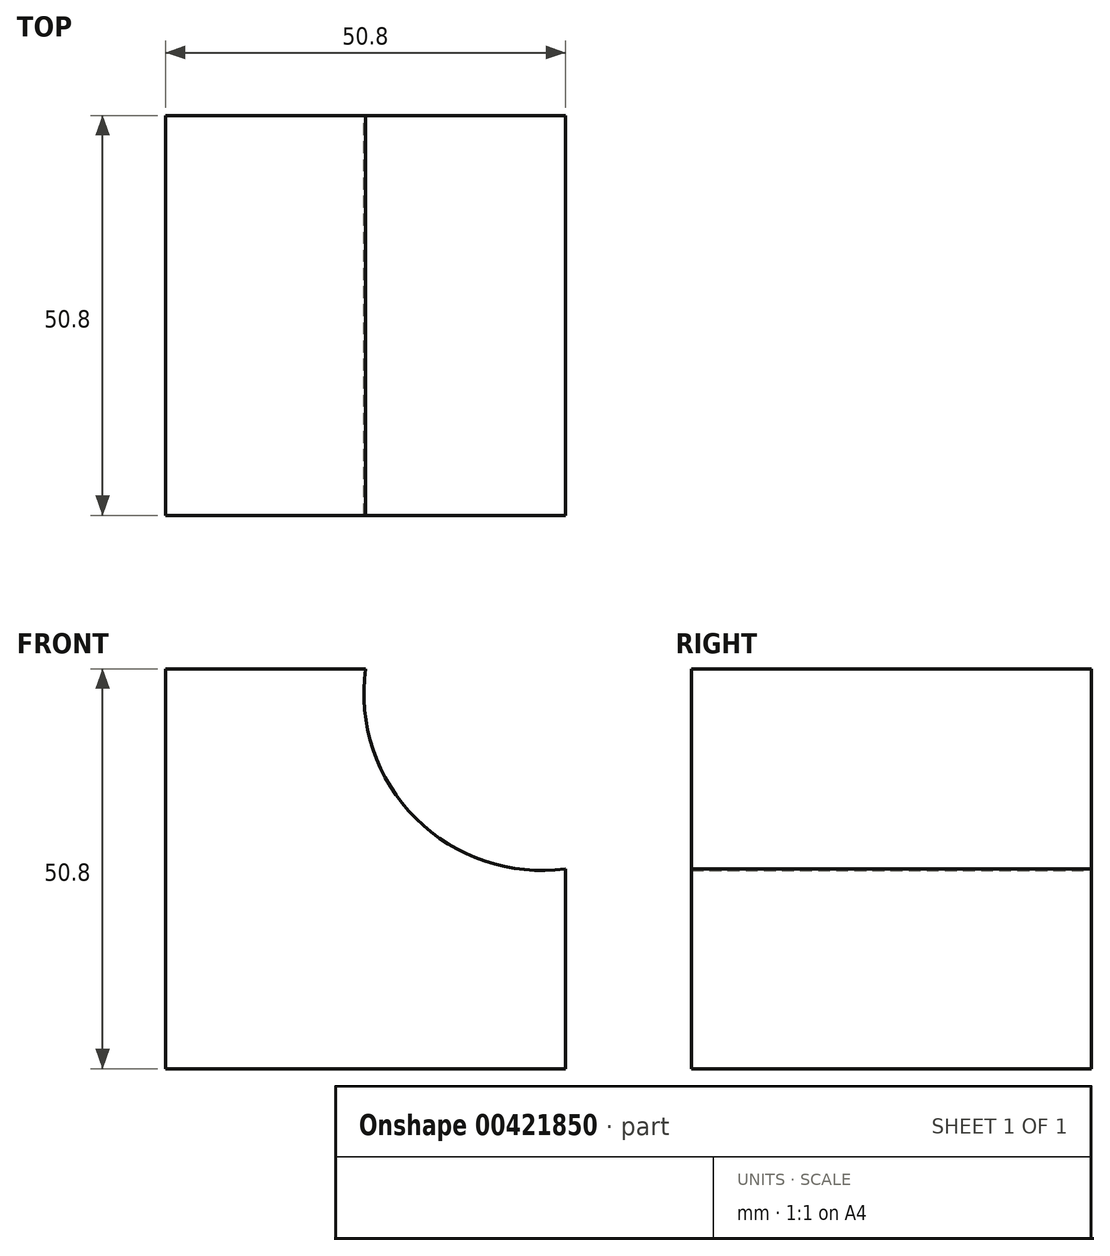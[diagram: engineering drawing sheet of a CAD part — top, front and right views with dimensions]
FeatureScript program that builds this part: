
annotation { "Feature Type Name" : "Feature", "Feature Type Description" : "" }
export const myFeature = defineFeature(function(context is Context, id is Id, definition is map)
    precondition{}
    {
        {
            var Q0;
            Q0=qCreatedBy(makeId("Front.planeOp"),FACE);
            var sketch = newSketch(context, id + "F0", { "sketchPlane" : qUnion([Q0])});
            skLineSegment(sketch, "E0", {"start": v(0, 0) * mm, "end": v(-50.8, 0) * mm});
            skLineSegment(sketch, "E1", {"start": v(-50.8, 0) * mm, "end": v(-50.8, 50.8) * mm});
            skLineSegment(sketch, "E2", {"start": v(-50.8, 50.8) * mm, "end": v(-25.4, 50.8) * mm});
            skLineSegment(sketch, "E3", {"start": v(0, 0) * mm, "end": v(0, 25.4) * mm});
            skArc(sketch, "E4", {"start": v(-25.4, 50.8) * mm, "mid": v(-19.01, 31.79) * mm, "end": v(0, 25.4) * mm});
            skSolve(sketch);
        }
        {
            var Q0;
            Q0=makeQuery(id+"F0.imprint","IMPRINT",FACE,{"disambiguationData":[TD([[makeQuery(id+"F0.imprint","IMPRINT",EDGE,{"derivedFrom":sQuery(id+"F0.wireOp",EDGE,"E0")}),-1.0]])]});
            extrude(context, id + "F1", {"entities" : qUnion([Q0]), "depth" : 50.8 * mm});
        }
    });
